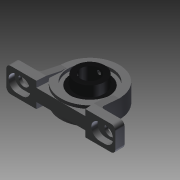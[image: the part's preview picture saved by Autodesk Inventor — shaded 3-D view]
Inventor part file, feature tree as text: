
AUTODESK INVENTOR PART (.ipt)
format: ipt  version: 2011 SP1 (Build 150282100, 282)  size: 305,152 bytes
history: native  units: mm
features: sketch x14, other x14, extrude x9, revolve x3, hole x2, thread x2
ambient origin geometry x8: Origin, YZ Plane, XZ Plane, XY Plane, X Axis, Y Axis, Z Axis, Center Point
bodies: Solid1 (feature_tree)
feature tree (44):
  extrude  "Extrusion1"  Depth=8.0mm TaperAngle=0.0deg
  extrude  "Extrusion2"  Depth=71.0mm TaperAngle=0.0deg
  extrude  "Extrusion3"  TaperAngle=360.0deg  [1 undecoded]
  extrude  "Extrusion4"  Depth=8.0mm TaperAngle=0.0deg
  extrude  "Extrusion5"  TaperAngle=360.0deg  [1 undecoded]
  revolve  "Revolution1"  [1 undecoded]
  extrude  "Extrusion6"  TaperAngle=360.0deg  [1 undecoded]
  extrude  "Extrusion7"  [1 undecoded]
  hole  "Hole1"  [1 undecoded]
  hole  "Hole2"  [1 undecoded]
  revolve  "Revolution2"  [1 undecoded]
  thread  "Thread1"  [1 undecoded]
  sketch  "Sketch_11"
  sketch  "Sketch_12"
  extrude  "Extrusion8"  [1 undecoded]
  extrude  "Extrusion9"  [1 undecoded]
  revolve  "Revolution3"  [1 undecoded]
  thread  "Thread2"  [1 undecoded]
  other  "to_screw_XY"
  other  "to_screw_YZ"
  other  "to_screw_ZX"
  other  "to_screw_X"
  other  "to_screw_Y"
  other  "to_screw_Z"
  other  "to_screw_Center"
  other  "to_screw_s_XY"
  other  "to_screw_s_YZ"
  other  "to_screw_s_ZX"
  other  "to_screw_s_X"
  other  "to_screw_s_Y"
  other  "to_screw_s_Z"
  other  "to_screw_s_Center"
  sketch  "Sketch_1"  dims[d0=16.0mm d1=0.0mm d2=8.0mm d3=0.0mm]
  sketch  "Sketch_2"  dims[d4=8.0mm d5=0.0mm d6=71.0mm d7=0.0mm]
  sketch  "Sketch_6"  dims[d22=7.0mm d23=6.0mm d24=4.0mm d25=2.0mm d26=90.0deg d27=8.0mm d28=0.0mm d29=360.0deg]
  sketch  "Sketch_3"  dims[d8=6.0mm d9=0.0mm d10=360.0deg]
  sketch  "Sketch_4"  dims[d11=8.0mm d12=0.0mm d13=8.0mm d14=0.0mm]
  sketch  "Sketch_5"  dims[d15=7.0mm d16=6.0mm d17=4.0mm d18=2.0mm d19=90.0deg d20=8.0mm d21=0.0mm]
  sketch  "Sketch_7"  dims[d30=3.459mm d31=0.0mm d32=4.0mm d33=0.0mm]
  sketch  "Sketch_8"  dims[d34=4.0mm d35=0.0mm d36=360.0deg]
  sketch  "Sketch9"  dims[d37=3.459mm d38=0.0mm]
  sketch  "Sketch10"
  sketch  "Sketch_13"
  sketch  "Sketch_21"
note: 13 required parameter values undecoded (feature->parameter linkage not recoverable at this tier; creation-order binding heuristic only, values carry confidence <= 0.55)